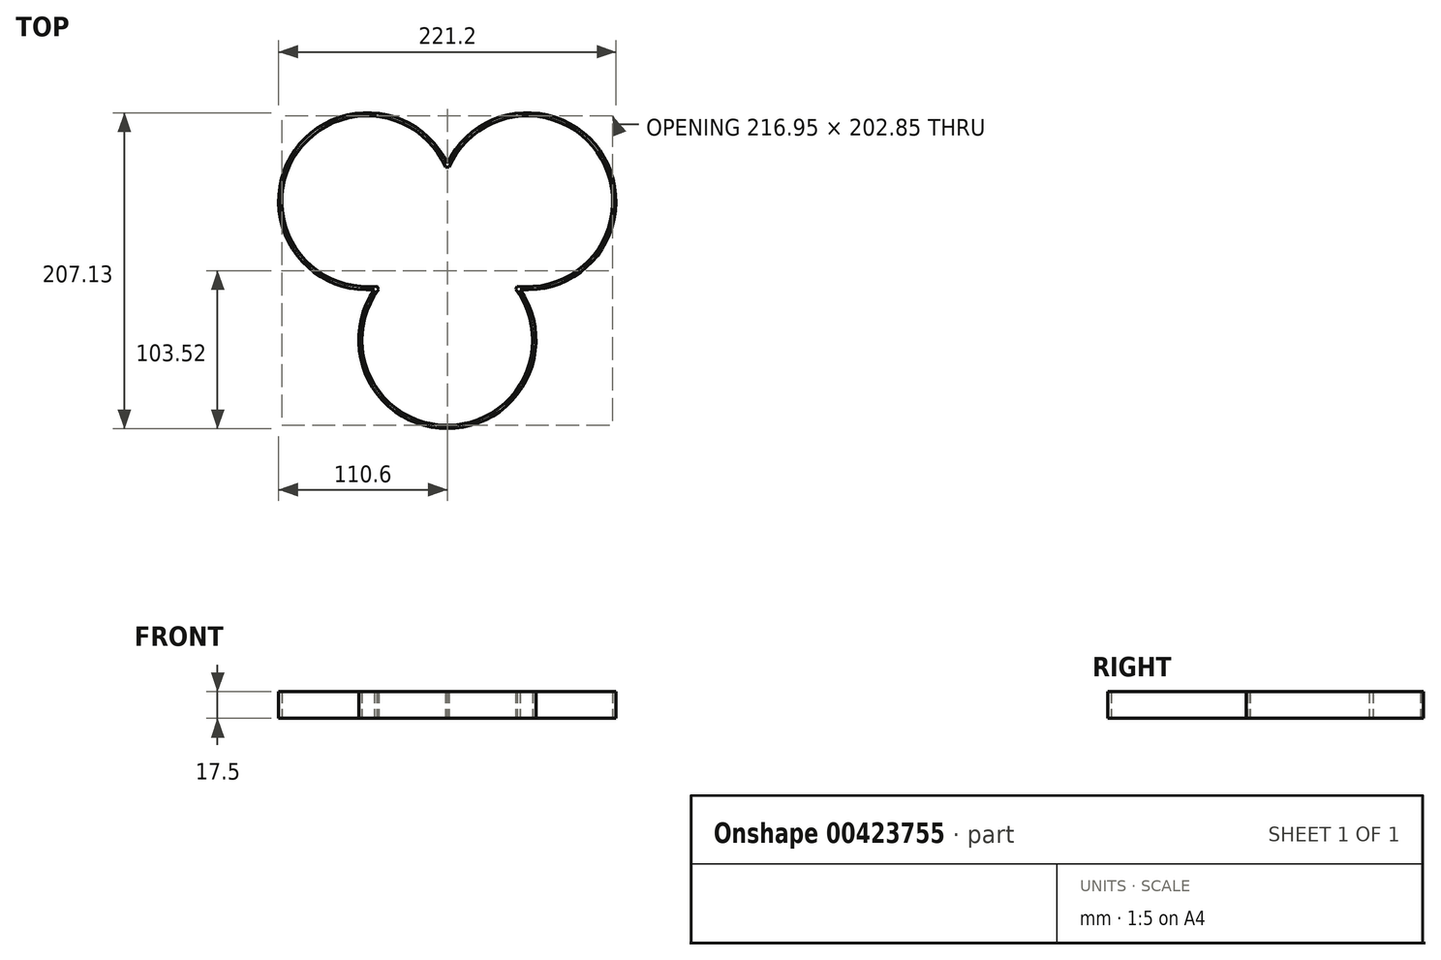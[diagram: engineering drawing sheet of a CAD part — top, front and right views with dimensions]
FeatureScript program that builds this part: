
annotation { "Feature Type Name" : "Feature", "Feature Type Description" : "" }
export const myFeature = defineFeature(function(context is Context, id is Id, definition is map)
    precondition{}
    {
        {
            var Q0;
            Q0=qCreatedBy(makeId("Top.planeOp"),FACE);
            var sketch = newSketch(context, id + "F0", { "sketchPlane" : qUnion([Q0])});
            skPoint(sketch, "E0.0.midPoint", {"position": v(68.29, 82.73) * mm});
            skArc(sketch, "E1", {"start": v(66.66, 114.62) * mm, "mid": v(-76, 122.7) * mm, "end": v(2.4, 3.25) * mm});
            skArc(sketch, "E2", {"start": v(133.81, 3.3) * mm, "mid": v(212.67, 122.55) * mm, "end": v(69.92, 114.62) * mm});
            skArc(sketch, "E3", {"start": v(3.99, 0.42) * mm, "mid": v(68.29, -127.18) * mm, "end": v(132.6, 0.42) * mm});
            skPoint(sketch, "E0.cCircle.center.orphan", {"position": v(68.29, 39.43) * mm});
            skArc(sketch, "E4.0", {"start": v(136.58, 0) * mm, "mid": v(215.17, 124.23) * mm, "end": v(68.29, 118.28) * mm});
            skArc(sketch, "E5.0", {"start": v(0, 0) * mm, "mid": v(68.29, -130.18) * mm, "end": v(136.58, 0) * mm});
            skArc(sketch, "E5.1", {"start": v(68.29, 118.28) * mm, "mid": v(-78.6, 124.23) * mm, "end": v(0, 0) * mm});
            skLineSegment(sketch, "E6", {"start": v(66.66, 114.62) * mm, "end": v(69.92, 114.62) * mm});
            skLineSegment(sketch, "E7", {"start": v(132.6, 0.42) * mm, "end": v(133.81, 3.3) * mm});
            skLineSegment(sketch, "E8", {"start": v(3.99, 0.42) * mm, "end": v(2.4, 3.25) * mm});
            skSolve(sketch);
        }
        {
            var Q0;
            Q0=makeQuery(id+"F0.imprint","IMPRINT",FACE,{"disambiguationData":[TD([[makeQuery(id+"F0.imprint","IMPRINT",EDGE,{"derivedFrom":sQuery(id+"F0.wireOp",EDGE,"E1")}),-1.0]])]});
            extrude(context, id + "F1", {"entities" : qUnion([Q0]), "depth" : 25 * mm});
        }
        {
            var Q0;
            Q0=makeQuery(id+"F1.opExtrude","SWEPT_BODY",BODY,{"disambiguationData":[OSD([sQuery(id+"F0.wireOp",EDGE,"E1"),sQuery(id+"F0.wireOp",EDGE,"E2"),sQuery(id+"F0.wireOp",EDGE,"E3"),sQuery(id+"F0.wireOp",EDGE,"E5.0"),sQuery(id+"F0.wireOp",EDGE,"E4.0"),sQuery(id+"F0.wireOp",EDGE,"E5.1"),sQuery(id+"F0.wireOp",EDGE,"E6"),sQuery(id+"F0.wireOp",EDGE,"E7"),sQuery(id+"F0.wireOp",EDGE,"E8")])]});
            var Q1;
            Q1=qCreatedBy(makeId("Origin.pointOp"),VERTEX);
            transform(context, id + "F2", {"entities" : qUnion([Q0]), "transformType" : TransformType.SCALE_UNIFORMLY, "scale" : 0.7, "scalePoint" : qUnion([Q1]), "makeCopy" : false});
        }
    });
